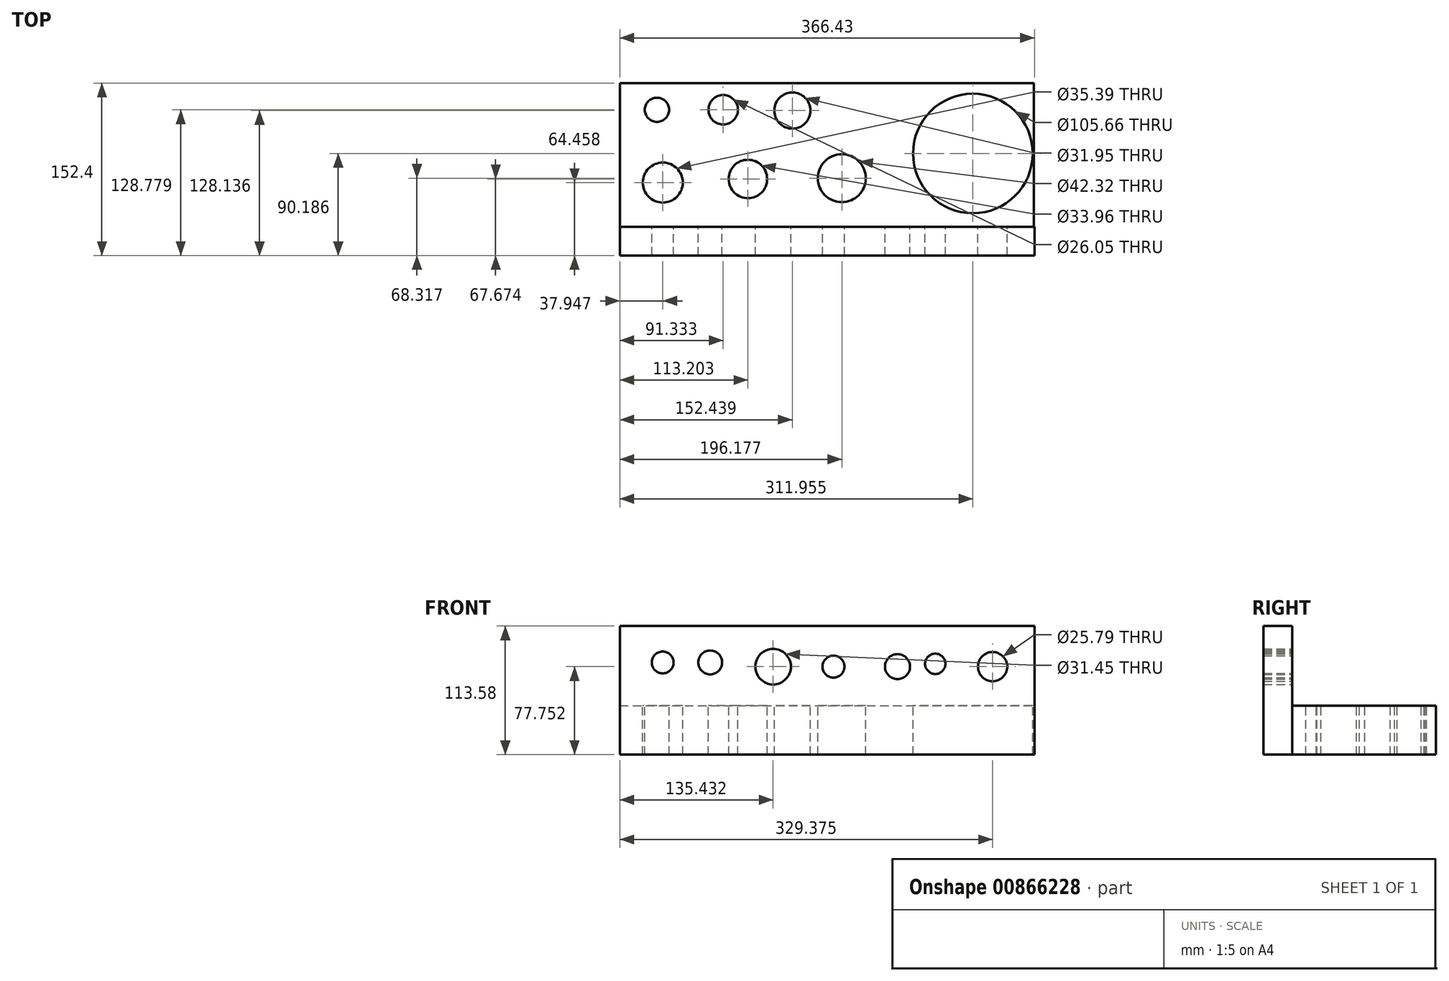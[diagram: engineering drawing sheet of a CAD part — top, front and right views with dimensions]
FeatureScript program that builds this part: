
annotation { "Feature Type Name" : "Feature", "Feature Type Description" : "" }
export const myFeature = defineFeature(function(context is Context, id is Id, definition is map)
    precondition{}
    {
        {
            var Q0;
            Q0=qCreatedBy(makeId("Front.planeOp"),FACE);
            var sketch = newSketch(context, id + "F0", { "sketchPlane" : qUnion([Q0])});
            skLineSegment(sketch, "E0.bottom", {"start": v(-188.78, 90.7) * mm, "end": v(177.2, 90.7) * mm});
            skLineSegment(sketch, "E0.top", {"start": v(-188.78, 47.6) * mm, "end": v(177.2, 47.6) * mm});
            skLineSegment(sketch, "E0.left", {"start": v(-188.78, 90.7) * mm, "end": v(-188.78, 47.6) * mm});
            skLineSegment(sketch, "E0.right", {"start": v(177.2, 90.7) * mm, "end": v(177.2, 47.6) * mm});
            skSolve(sketch);
        }
        {
            var Q0;
            Q0=makeQuery(id+"F0.imprint","IMPRINT",FACE,{"disambiguationData":[TD([[makeQuery(id+"F0.imprint","IMPRINT",EDGE,{"derivedFrom":sQuery(id+"F0.wireOp",EDGE,"E0.bottom")}),-1.0]])]});
            extrude(context, id + "F1", {"entities" : qUnion([Q0]), "depth" : 127 * mm, "offsetDistance" : 25.4 * mm});
        }
        {
            var Q0;
            Q0=makeQuery(id+"F1.opExtrude","SWEPT_FACE",FACE,{"disambiguationData":[OSD([sQuery(id+"F0.wireOp",EDGE,"E0.bottom")])]});
            var sketch = newSketch(context, id + "F2", { "sketchPlane" : qUnion([Q0])});
            skCircle(sketch, "E1", {"center": v(-155.98, -23.62) * mm, "radius": 10.7 * mm});
            skCircle(sketch, "E2", {"center": v(-97.45, -23.62) * mm, "radius": 13.02 * mm});
            skCircle(sketch, "E3", {"center": v(-36.34, -24.26) * mm, "radius": 15.98 * mm});
            skCircle(sketch, "E4", {"center": v(123.18, -62.21) * mm, "radius": 52.83 * mm});
            skCircle(sketch, "E5", {"center": v(7.4, -84.08) * mm, "radius": 21.16 * mm});
            skCircle(sketch, "E6", {"center": v(-150.83, -87.94) * mm, "radius": 17.7 * mm});
            skCircle(sketch, "E7", {"center": v(-75.58, -84.73) * mm, "radius": 16.98 * mm});
            skSolve(sketch);
        }
        {
            var Q0;
            Q0=makeQuery(id+"F2.imprint","IMPRINT",FACE,{"disambiguationData":[TD([[makeQuery(id+"F2.imprint","IMPRINT",EDGE,{"derivedFrom":sQuery(id+"F2.wireOp",EDGE,"E6")}),1.0]])]});
            var Q1;
            Q1=makeQuery(id+"F2.imprint","IMPRINT",FACE,{"disambiguationData":[TD([[makeQuery(id+"F2.imprint","IMPRINT",EDGE,{"derivedFrom":sQuery(id+"F2.wireOp",EDGE,"E1")}),1.0]])]});
            var Q2;
            Q2=makeQuery(id+"F2.imprint","IMPRINT",FACE,{"disambiguationData":[TD([[makeQuery(id+"F2.imprint","IMPRINT",EDGE,{"derivedFrom":sQuery(id+"F2.wireOp",EDGE,"E2")}),1.0]])]});
            var Q3;
            Q3=makeQuery(id+"F2.imprint","IMPRINT",FACE,{"disambiguationData":[TD([[makeQuery(id+"F2.imprint","IMPRINT",EDGE,{"derivedFrom":sQuery(id+"F2.wireOp",EDGE,"E7")}),1.0]])]});
            var Q4;
            Q4=makeQuery(id+"F2.imprint","IMPRINT",FACE,{"disambiguationData":[TD([[makeQuery(id+"F2.imprint","IMPRINT",EDGE,{"derivedFrom":sQuery(id+"F2.wireOp",EDGE,"E5")}),1.0]])]});
            var Q5;
            Q5=makeQuery(id+"F2.imprint","IMPRINT",FACE,{"disambiguationData":[TD([[makeQuery(id+"F2.imprint","IMPRINT",EDGE,{"derivedFrom":sQuery(id+"F2.wireOp",EDGE,"E3")}),1.0]])]});
            var Q6;
            Q6=makeQuery(id+"F2.imprint","IMPRINT",FACE,{"disambiguationData":[TD([[makeQuery(id+"F2.imprint","IMPRINT",EDGE,{"derivedFrom":sQuery(id+"F2.wireOp",EDGE,"E4")}),1.0]])]});
            extrude(context, id + "F3", {"entities" : qUnion([Q0, Q1, Q2, Q3, Q4, Q5, Q6]), "operationType" : NewBodyOperationType.REMOVE, "oppositeDirection" : true, "depth" : 254 * mm, "offsetDistance" : 25.4 * mm});
        }
        {
            var Q0;
            Q0=makeQuery(id+"F1.opExtrude","CAP_FACE",FACE,{"disambiguationData":[OSD([sQuery(id+"F0.wireOp",EDGE,"E0.bottom"),sQuery(id+"F0.wireOp",EDGE,"E0.top"),sQuery(id+"F0.wireOp",EDGE,"E0.left"),sQuery(id+"F0.wireOp",EDGE,"E0.right")])],"isStart":false});
            var sketch = newSketch(context, id + "F4", { "sketchPlane" : qUnion([Q0])});
            skLineSegment(sketch, "E8.bottom", {"start": v(-188.78, 47.6) * mm, "end": v(177.65, 47.6) * mm});
            skLineSegment(sketch, "E8.top", {"start": v(-188.78, 161.18) * mm, "end": v(177.65, 161.18) * mm});
            skLineSegment(sketch, "E8.left", {"start": v(-188.78, 47.6) * mm, "end": v(-188.78, 161.18) * mm});
            skLineSegment(sketch, "E8.right", {"start": v(177.65, 47.6) * mm, "end": v(177.65, 161.18) * mm});
            skCircle(sketch, "E9", {"center": v(-150.94, 129.06) * mm, "radius": 9.65 * mm});
            skCircle(sketch, "E10", {"center": v(-108.94, 129.06) * mm, "radius": 10.55 * mm});
            skCircle(sketch, "E11", {"center": v(89.95, 127.82) * mm, "radius": 9 * mm});
            skCircle(sketch, "E12", {"center": v(56.6, 125.35) * mm, "radius": 11.05 * mm});
            skCircle(sketch, "E13", {"center": v(0, 125.35) * mm, "radius": 9.73 * mm});
            skCircle(sketch, "E14", {"center": v(140.6, 125.35) * mm, "radius": 12.9 * mm});
            skCircle(sketch, "E15", {"center": v(-53.35, 125.35) * mm, "radius": 15.72 * mm});
            skSolve(sketch);
        }
        {
            var Q0;
            Q0 = qSketchRegion(id + "F4", true);
            extrude(context, id + "F5", {"entities" : qUnion([Q0]), "operationType" : NewBodyOperationType.ADD, "depth" : 25.4 * mm, "offsetDistance" : 25.4 * mm});
        }
    });
